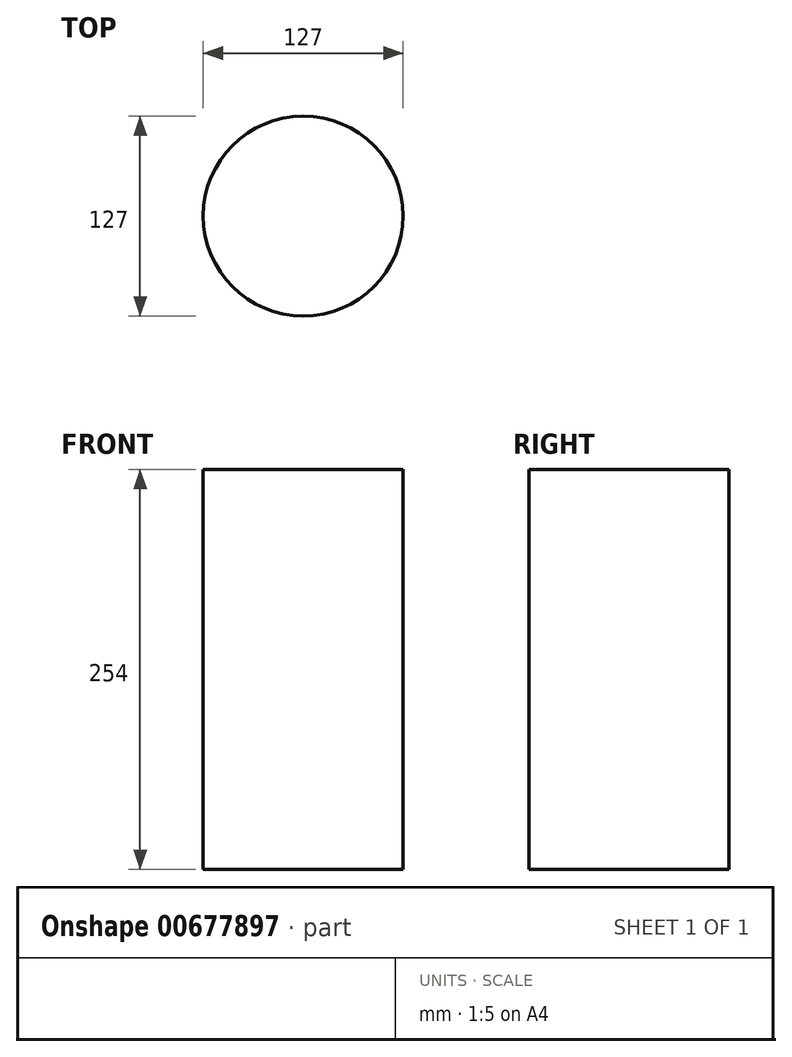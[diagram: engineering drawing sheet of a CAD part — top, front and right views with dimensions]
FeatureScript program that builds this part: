
annotation { "Feature Type Name" : "Feature", "Feature Type Description" : "" }
export const myFeature = defineFeature(function(context is Context, id is Id, definition is map)
    precondition{}
    {
        {
            var Q0;
            Q0=qCreatedBy(makeId("Top.planeOp"),FACE);
            var sketch = newSketch(context, id + "F0", { "sketchPlane" : qUnion([Q0])});
            skCircle(sketch, "E0", {"center": v(0, 0) * mm, "radius": 63.5 * mm});
            skSolve(sketch);
        }
        {
            var Q0;
            Q0 = qSketchRegion(id + "F0", true);
            extrude(context, id + "F1", {"entities" : qUnion([Q0]), "depth" : 254 * mm, "offsetDistance" : 25.4 * mm});
        }
    });
